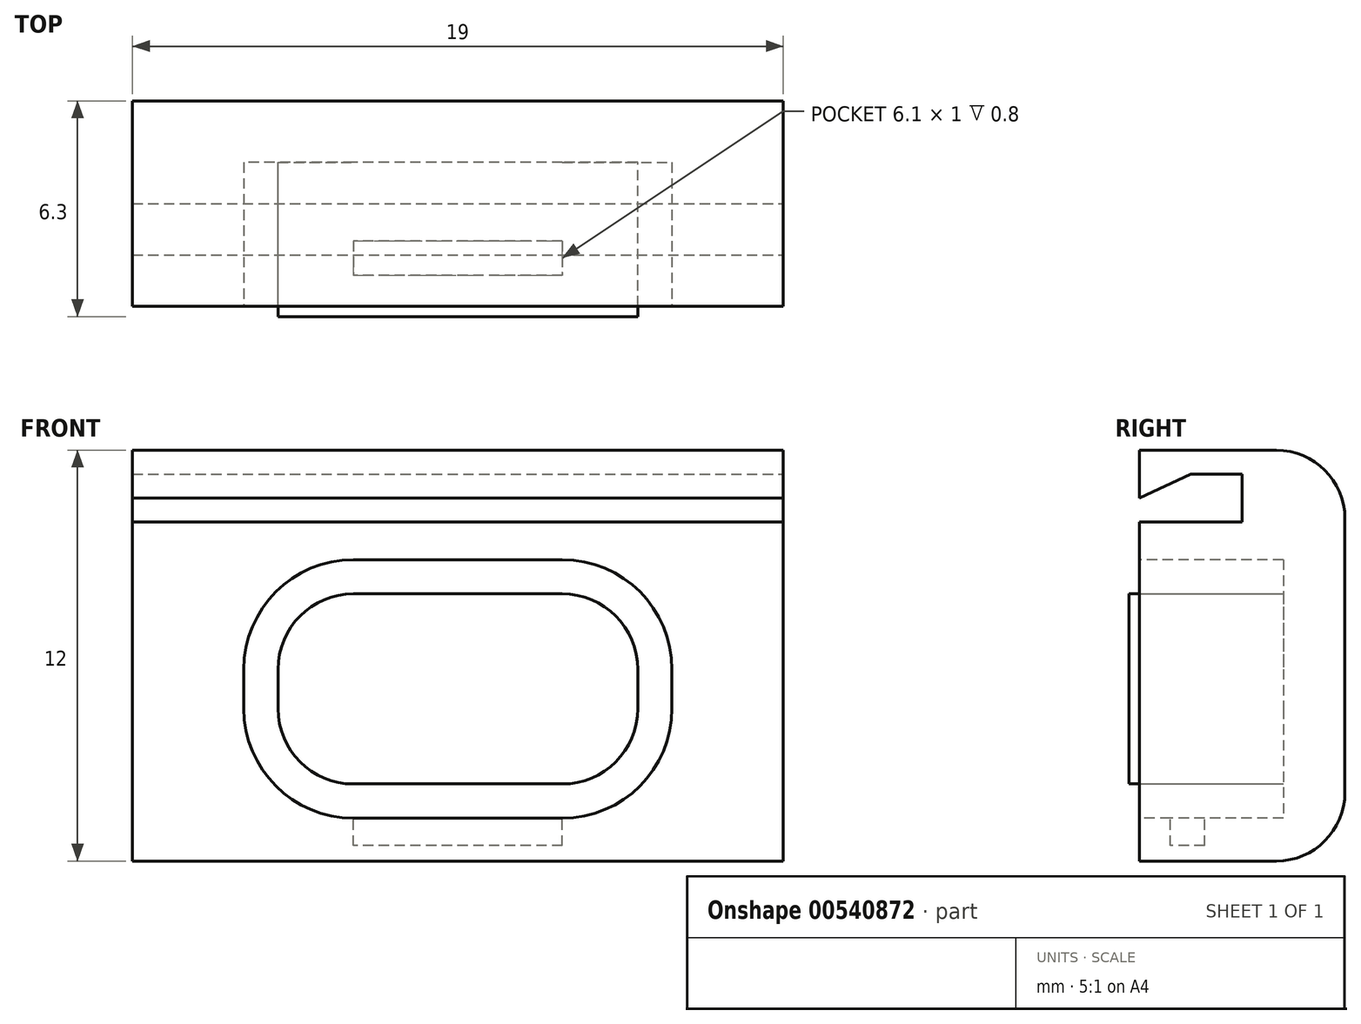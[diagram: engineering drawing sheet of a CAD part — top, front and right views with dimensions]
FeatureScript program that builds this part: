
annotation { "Feature Type Name" : "Feature", "Feature Type Description" : "" }
export const myFeature = defineFeature(function(context is Context, id is Id, definition is map)
    precondition{}
    {
        {
            var Q0;
            Q0=qCreatedBy(makeId("Front.planeOp"),FACE);
            var sketch = newSketch(context, id + "F0", { "sketchPlane" : qUnion([Q0])});
            skLineSegment(sketch, "E0.bottom", {"start": v(9.5, 6) * mm, "end": v(-9.5, 6) * mm});
            skLineSegment(sketch, "E0.top", {"start": v(9.5, -6) * mm, "end": v(-9.5, -6) * mm});
            skLineSegment(sketch, "E0.left", {"start": v(9.5, 6) * mm, "end": v(9.5, -6) * mm});
            skLineSegment(sketch, "E0.right", {"start": v(-9.5, 6) * mm, "end": v(-9.5, -6) * mm});
            skPoint(sketch, "E0.middle", {"position": v(0, 0) * mm});
            skSolve(sketch);
        }
        {
            var Q0;
            Q0=makeQuery(id+"F0.imprint","IMPRINT",FACE,{"disambiguationData":[TD([[makeQuery(id+"F0.imprint","IMPRINT",EDGE,{"derivedFrom":sQuery(id+"F0.wireOp",EDGE,"E0.bottom")}),1.0]])]});
            extrude(context, id + "F1", {"entities" : qUnion([Q0]), "depth" : 6 * mm, "offsetDistance" : 25 * mm});
        }
        {
            var Q0;
            Q0=makeQuery(id+"F1.opExtrude","CAP_FACE",FACE,{"disambiguationData":[OSD([sQuery(id+"F0.wireOp",EDGE,"E0.bottom"),sQuery(id+"F0.wireOp",EDGE,"E0.top"),sQuery(id+"F0.wireOp",EDGE,"E0.left"),sQuery(id+"F0.wireOp",EDGE,"E0.right")])],"isStart":false});
            var sketch = newSketch(context, id + "F2", { "sketchPlane" : qUnion([Q0])});
            skLineSegment(sketch, "E1.bottom", {"start": v(3.05, 2.8) * mm, "end": v(-3.05, 2.8) * mm});
            skLineSegment(sketch, "E1.top", {"start": v(3.05, -4.75) * mm, "end": v(-3.05, -4.75) * mm});
            skLineSegment(sketch, "E1.left", {"start": v(6.25, -0.4) * mm, "end": v(6.25, -1.55) * mm});
            skLineSegment(sketch, "E1.right", {"start": v(-6.25, -0.4) * mm, "end": v(-6.25, -1.55) * mm});
            skPoint(sketch, "E1.middle", {"position": v(0, -0.97) * mm});
            skPoint(sketch, "E2.visualSharp", {"position": v(-6.25, 2.8) * mm});
            skArc(sketch, "E2.filletArc", {"start": v(-3.05, 2.8) * mm, "mid": v(-5.31, 1.86) * mm, "end": v(-6.25, -0.4) * mm});
            skPoint(sketch, "E3.visualSharp", {"position": v(6.25, 2.8) * mm});
            skArc(sketch, "E3.filletArc", {"start": v(6.25, -0.4) * mm, "mid": v(5.31, 1.86) * mm, "end": v(3.05, 2.8) * mm});
            skPoint(sketch, "E4.visualSharp", {"position": v(-6.25, -4.75) * mm});
            skArc(sketch, "E4.filletArc", {"start": v(-6.25, -1.55) * mm, "mid": v(-5.31, -3.81) * mm, "end": v(-3.05, -4.75) * mm});
            skPoint(sketch, "E5.visualSharp", {"position": v(6.25, -4.75) * mm});
            skArc(sketch, "E5.filletArc", {"start": v(3.05, -4.75) * mm, "mid": v(5.31, -3.81) * mm, "end": v(6.25, -1.55) * mm});
            skLineSegment(sketch, "E6", {"start": v(-9.5, 3.9) * mm, "end": v(9.5, 3.9) * mm});
            skLineSegment(sketch, "E7.0.0", {"start": v(-9.5, -6) * mm, "end": v(9.5, -6) * mm});
            skLineSegment(sketch, "E7.0.1", {"start": v(9.5, -6) * mm, "end": v(9.5, 6) * mm});
            skLineSegment(sketch, "E7.0.2", {"start": v(9.5, 6) * mm, "end": v(-9.5, 6) * mm});
            skLineSegment(sketch, "E7.0.3", {"start": v(-9.5, 6) * mm, "end": v(-9.5, -6) * mm});
            skSolve(sketch);
        }
        {
            var Q0;
            Q0=makeQuery(id+"F2.imprint","IMPRINT",FACE,{"disambiguationData":[TD([[makeQuery(id+"F2.imprint","IMPRINT",EDGE,{"derivedFrom":sQuery(id+"F2.wireOp",EDGE,"E1.bottom")}),1.0]])]});
            extrude(context, id + "F3", {"entities" : qUnion([Q0]), "operationType" : NewBodyOperationType.REMOVE, "oppositeDirection" : true, "depth" : 4.2 * mm, "offsetDistance" : 25 * mm});
        }
        {
            var Q0;
            {var subQ0=sQuery(id+"F2.wireOp",EDGE,"E6");Q0=makeQuery(id+"F2.imprint","IMPRINT",FACE,{"disambiguationData":[TD([[makeQuery(id+"F2.imprint","IMPRINT",EDGE,{"derivedFrom":subQ0}),1.0]])]});}
            extrude(context, id + "F4", {"entities" : qUnion([Q0]), "operationType" : NewBodyOperationType.REMOVE, "oppositeDirection" : true, "depth" : 3 * mm, "offsetDistance" : 25 * mm});
        }
        {
            var Q0;
            Q0=makeQuery(id+"F1.opExtrude","SWEPT_FACE",FACE,{"disambiguationData":[OSD([sQuery(id+"F0.wireOp",EDGE,"E0.left")])]});
            var sketch = newSketch(context, id + "F5", { "sketchPlane" : qUnion([Q0])});
            skLineSegment(sketch, "E8.bottom", {"start": v(-3, 6) * mm, "end": v(-6, 6) * mm});
            skLineSegment(sketch, "E8.top", {"start": v(-3, 5.3) * mm, "end": v(-6, 5.3) * mm});
            skLineSegment(sketch, "E8.left", {"start": v(-3, 6) * mm, "end": v(-3, 5.3) * mm});
            skLineSegment(sketch, "E8.right", {"start": v(-6, 6) * mm, "end": v(-6, 5.3) * mm});
            skLineSegment(sketch, "E9", {"start": v(-6, 5.3) * mm, "end": v(-6, 4.6) * mm});
            skLineSegment(sketch, "E10", {"start": v(-6, 4.6) * mm, "end": v(-4.5, 5.3) * mm});
            skSolve(sketch);
        }
        {
            var Q0;
            Q0=makeQuery(id+"F5.imprint","IMPRINT",FACE,{"disambiguationData":[TD([[makeQuery(id+"F5.imprint","IMPRINT",EDGE,{"derivedFrom":sQuery(id+"F5.wireOp",EDGE,"E8.bottom")}),1.0]])]});
            var Q1;
            {var subQ0=sQuery(id+"F5.wireOp",EDGE,"E9");Q1=makeQuery(id+"F5.imprint","IMPRINT",FACE,{"disambiguationData":[TD([[makeQuery(id+"F5.imprint","IMPRINT",EDGE,{"derivedFrom":subQ0}),1.0]])]});}
            var Q2;
            Q2=makeQuery(id+"F1.opExtrude","SWEPT_FACE",FACE,{"disambiguationData":[OSD([sQuery(id+"F0.wireOp",EDGE,"E0.right")])]});
            extrude(context, id + "F6", {"entities" : qUnion([Q0, Q1]), "operationType" : NewBodyOperationType.ADD, "endBound" : BoundingType.UP_TO_SURFACE, "oppositeDirection" : true, "depth" : 25 * mm, "endBoundEntityFace" : qUnion([Q2]), "offsetDistance" : 25 * mm});
        }
        {
            var Q0;
            Q0=makeQuery(id+"F1.opExtrude","CAP_EDGE",EDGE,{"disambiguationData":[OSD([sQuery(id+"F0.wireOp",EDGE,"E0.bottom")])],"isStart":true});
            var Q1;
            Q1=makeQuery(id+"F1.opExtrude","CAP_EDGE",EDGE,{"disambiguationData":[OSD([sQuery(id+"F0.wireOp",EDGE,"E0.top")])],"isStart":true});
            fillet(context, id + "F7", {"entities" : qUnion([Q0, Q1]), "radius" : 2 * mm, "tangentPropagation" : true, "allowEdgeOverflow" : false});
        }
        {
            var Q0;
            Q0=makeQuery(id+"F3.boolean.opBoolean","COPY",FACE,{"derivedFrom":makeQuery(id+"F3.opExtrude","SWEPT_FACE",FACE,{"disambiguationData":[OSD([sQuery(id+"F2.wireOp",EDGE,"E1.top")])]})});
            var sketch = newSketch(context, id + "F8", { "sketchPlane" : qUnion([Q0])});
            skLineSegment(sketch, "E11.bottom", {"start": v(3.05, -5.1) * mm, "end": v(-3.05, -5.1) * mm});
            skLineSegment(sketch, "E11.top", {"start": v(3.05, -4.1) * mm, "end": v(-3.05, -4.1) * mm});
            skLineSegment(sketch, "E11.left", {"start": v(3.05, -5.1) * mm, "end": v(3.05, -4.1) * mm});
            skLineSegment(sketch, "E11.right", {"start": v(-3.05, -5.1) * mm, "end": v(-3.05, -4.1) * mm});
            skSolve(sketch);
        }
        {
            var Q0;
            Q0 = qSketchRegion(id + "F8", true);
            extrude(context, id + "F9", {"entities" : qUnion([Q0]), "operationType" : NewBodyOperationType.REMOVE, "oppositeDirection" : true, "depth" : 0.8 * mm, "offsetDistance" : 25 * mm});
        }
        {
            var Q0;
            Q0=makeQuery(id+"F3.boolean.opBoolean","COPY",FACE,{"derivedFrom":makeQuery(id+"F3.opExtrude","CAP_FACE",FACE,{"disambiguationData":[OSD([sQuery(id+"F2.wireOp",EDGE,"E1.bottom"),sQuery(id+"F2.wireOp",EDGE,"E1.top"),sQuery(id+"F2.wireOp",EDGE,"E1.left"),sQuery(id+"F2.wireOp",EDGE,"E1.right"),sQuery(id+"F2.wireOp",EDGE,"E2.filletArc"),sQuery(id+"F2.wireOp",EDGE,"E3.filletArc"),sQuery(id+"F2.wireOp",EDGE,"E4.filletArc"),sQuery(id+"F2.wireOp",EDGE,"E5.filletArc")])],"isStart":false})});
            var sketch = newSketch(context, id + "F10", { "sketchPlane" : qUnion([Q0])});
            skArc(sketch, "E12.0", {"start": v(-5.25, -1.55) * mm, "mid": v(-4.6, -3.1) * mm, "end": v(-3.05, -3.75) * mm});
            skLineSegment(sketch, "E12.1", {"start": v(-5.25, -0.4) * mm, "end": v(-5.25, -1.55) * mm});
            skLineSegment(sketch, "E12.2", {"start": v(-3.05, -3.75) * mm, "end": v(3.05, -3.75) * mm});
            skArc(sketch, "E12.3", {"start": v(-3.05, 1.8) * mm, "mid": v(-4.6, 1.16) * mm, "end": v(-5.25, -0.4) * mm});
            skArc(sketch, "E12.4", {"start": v(3.05, -3.75) * mm, "mid": v(4.6, -3.1) * mm, "end": v(5.25, -1.55) * mm});
            skLineSegment(sketch, "E12.5", {"start": v(5.25, -1.55) * mm, "end": v(5.25, -0.4) * mm});
            skArc(sketch, "E12.6", {"start": v(5.25, -0.4) * mm, "mid": v(4.6, 1.16) * mm, "end": v(3.05, 1.8) * mm});
            skLineSegment(sketch, "E12.7", {"start": v(3.05, 1.8) * mm, "end": v(-3.05, 1.8) * mm});
            skSolve(sketch);
        }
        {
            var Q0;
            Q0=makeQuery(id+"F10.imprint","IMPRINT",FACE,{"disambiguationData":[TD([[makeQuery(id+"F10.imprint","IMPRINT",EDGE,{"derivedFrom":sQuery(id+"F10.wireOp",EDGE,"E12.0")}),1.0]])]});
            extrude(context, id + "F11", {"entities" : qUnion([Q0]), "operationType" : NewBodyOperationType.ADD, "depth" : 4.5 * mm, "offsetDistance" : 25 * mm});
        }
    });
